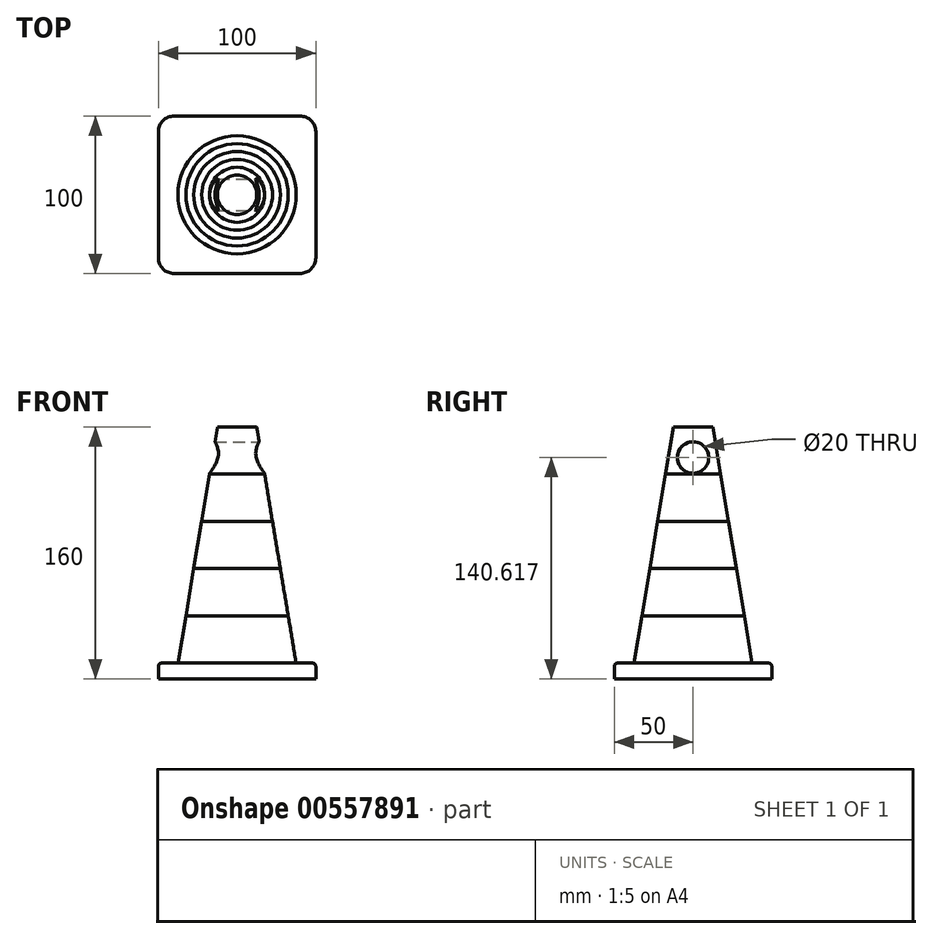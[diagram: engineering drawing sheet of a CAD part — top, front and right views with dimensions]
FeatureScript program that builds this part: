
annotation { "Feature Type Name" : "Feature", "Feature Type Description" : "" }
export const myFeature = defineFeature(function(context is Context, id is Id, definition is map)
    precondition{}
    {
        {
            var Q0;
            Q0=qCreatedBy(makeId("Top.planeOp"),FACE);
            var sketch = newSketch(context, id + "F0", { "sketchPlane" : qUnion([Q0])});
            skLineSegment(sketch, "E0.bottom", {"start": v(-40, 50) * mm, "end": v(40, 50) * mm});
            skLineSegment(sketch, "E0.top", {"start": v(-40, -50) * mm, "end": v(40, -50) * mm});
            skLineSegment(sketch, "E0.left", {"start": v(-50, 40) * mm, "end": v(-50, -40) * mm});
            skLineSegment(sketch, "E0.right", {"start": v(50, 40) * mm, "end": v(50, -40) * mm});
            skPoint(sketch, "E1.visualSharp", {"position": v(-50, 50) * mm});
            skArc(sketch, "E1.filletArc", {"start": v(-40, 50) * mm, "mid": v(-47.07, 47.07) * mm, "end": v(-50, 40) * mm});
            skPoint(sketch, "E2.visualSharp", {"position": v(50, 50) * mm});
            skArc(sketch, "E2.filletArc", {"start": v(50, 40) * mm, "mid": v(47.07, 47.07) * mm, "end": v(40, 50) * mm});
            skPoint(sketch, "E3.visualSharp", {"position": v(50, -50) * mm});
            skArc(sketch, "E3.filletArc", {"start": v(40, -50) * mm, "mid": v(47.07, -47.07) * mm, "end": v(50, -40) * mm});
            skPoint(sketch, "E4.visualSharp", {"position": v(-50, -50) * mm});
            skArc(sketch, "E4.filletArc", {"start": v(-50, -40) * mm, "mid": v(-47.07, -47.07) * mm, "end": v(-40, -50) * mm});
            skSolve(sketch);
        }
        {
            var Q0;
            Q0=makeQuery(id+"F0.imprint","IMPRINT",FACE,{"disambiguationData":[TD([[makeQuery(id+"F0.imprint","IMPRINT",EDGE,{"derivedFrom":sQuery(id+"F0.wireOp",EDGE,"E0.bottom")}),-1.0]])]});
            extrude(context, id + "F1", {"entities" : qUnion([Q0]), "depth" : 10 * mm});
        }
        {
            var Q0;
            Q0=makeQuery(id+"F1.opExtrude","CAP_FACE",FACE,{"disambiguationData":[OSD([sQuery(id+"F0.wireOp",EDGE,"E0.bottom"),sQuery(id+"F0.wireOp",EDGE,"E0.top"),sQuery(id+"F0.wireOp",EDGE,"E0.left"),sQuery(id+"F0.wireOp",EDGE,"E0.right")])],"isStart":false});
            var sketch = newSketch(context, id + "F2", { "sketchPlane" : qUnion([Q0])});
            skLineSegment(sketch, "E5.0.0", {"start": v(-50, 40) * mm, "end": v(-50, -40) * mm});
            skLineSegment(sketch, "E5.0.1", {"start": v(-50, -50) * mm, "end": v(-40, -50) * mm});
            skLineSegment(sketch, "E5.0.2", {"start": v(50, -50) * mm, "end": v(50, 40) * mm});
            skLineSegment(sketch, "E5.0.3", {"start": v(50, 50) * mm, "end": v(-50, 50) * mm});
            skCircle(sketch, "E6", {"center": v(0, 0) * mm, "radius": 37.5 * mm});
            skSolve(sketch);
        }
        {
            var Q0;
            Q0=qCreatedBy(makeId("Top.planeOp"),FACE);
            cPlane(context, id + "F3", {"entities" : qUnion([Q0]), "cplaneType" : CPlaneType.OFFSET, "offset" : 40 * mm, "width" : 150 * mm, "height" : 150 * mm});
        }
        {
            var Q0;
            Q0=qCreatedBy(id+"F3.planeOp",FACE);
            var sketch = newSketch(context, id + "F4", { "sketchPlane" : qUnion([Q0])});
            skCircle(sketch, "E7.0", {"center": v(0, 0) * mm, "radius": 37.5 * mm});
            skCircle(sketch, "E8", {"center": v(0, 0) * mm, "radius": 32.5 * mm});
            skSolve(sketch);
        }
        {
            var Q1;
            Q1=makeQuery(id+"F2.imprint","IMPRINT",FACE,{"disambiguationData":[TD([[makeQuery(id+"F2.imprint","IMPRINT",EDGE,{"derivedFrom":sQuery(id+"F2.wireOp",EDGE,"E6")}),1.0]])]});
            var Q2;
            Q2=makeQuery(id+"F4.imprint","IMPRINT",FACE,{"disambiguationData":[TD([[makeQuery(id+"F4.imprint","IMPRINT",EDGE,{"derivedFrom":sQuery(id+"F4.wireOp",EDGE,"E8")}),1.0]])]});
            loft(context, id + "F5", {"sheetProfilesArray" : [{ "sheetProfileEntities" : qUnion([Q1]) }, { "sheetProfileEntities" : qUnion([Q2]) }]});
        }
        {
            var Q0;
            Q0=qCreatedBy(id+"F3.planeOp",FACE);
            cPlane(context, id + "F6", {"entities" : qUnion([Q0]), "cplaneType" : CPlaneType.OFFSET, "offset" : 30 * mm, "width" : 150 * mm, "height" : 150 * mm});
        }
        {
            var Q0;
            Q0=qCreatedBy(id+"F6.planeOp",FACE);
            var sketch = newSketch(context, id + "F7", { "sketchPlane" : qUnion([Q0])});
            skCircle(sketch, "E9.0.0", {"center": v(0, 0) * mm, "radius": 32.5 * mm});
            skCircle(sketch, "E10", {"center": v(0, 0) * mm, "radius": 27.5 * mm});
            skSolve(sketch);
        }
        {
            var Q1;
            Q1=makeQuery(id+"F5.opLoft","CAP_FACE",FACE,{"disambiguationData":[OSD([makeQuery(id+"F4.imprint","IMPRINT",FACE,{"disambiguationData":[TD([[makeQuery(id+"F4.imprint","IMPRINT",EDGE,{"derivedFrom":sQuery(id+"F4.wireOp",EDGE,"E8")}),1.0]])]})])],"isStart":true});
            var Q2;
            Q2=makeQuery(id+"F7.imprint","IMPRINT",FACE,{"disambiguationData":[TD([[makeQuery(id+"F7.imprint","IMPRINT",EDGE,{"derivedFrom":sQuery(id+"F7.wireOp",EDGE,"E10")}),1.0]])]});
            loft(context, id + "F8", {"sheetProfilesArray" : [{ "sheetProfileEntities" : qUnion([Q1]) }, { "sheetProfileEntities" : qUnion([Q2]) }]});
        }
        {
            var Q0;
            Q0=qCreatedBy(id+"F6.planeOp",FACE);
            cPlane(context, id + "F9", {"entities" : qUnion([Q0]), "cplaneType" : CPlaneType.OFFSET, "offset" : 30 * mm, "width" : 150 * mm, "height" : 150 * mm});
        }
        {
            var Q0;
            Q0=qCreatedBy(id+"F9.planeOp",FACE);
            var sketch = newSketch(context, id + "F10", { "sketchPlane" : qUnion([Q0])});
            skCircle(sketch, "E11.0.0", {"center": v(0, 0) * mm, "radius": 27.5 * mm});
            skCircle(sketch, "E12", {"center": v(0, 0) * mm, "radius": 22.5 * mm});
            skSolve(sketch);
        }
        {
            var Q1;
            Q1=makeQuery(id+"F8.opLoft","CAP_FACE",FACE,{"disambiguationData":[OSD([makeQuery(id+"F7.imprint","IMPRINT",FACE,{"disambiguationData":[TD([[makeQuery(id+"F7.imprint","IMPRINT",EDGE,{"derivedFrom":sQuery(id+"F7.wireOp",EDGE,"E10")}),1.0]])]})])],"isStart":true});
            var Q2;
            Q2=makeQuery(id+"F10.imprint","IMPRINT",FACE,{"disambiguationData":[TD([[makeQuery(id+"F10.imprint","IMPRINT",EDGE,{"derivedFrom":sQuery(id+"F10.wireOp",EDGE,"E12")}),1.0]])]});
            loft(context, id + "F11", {"sheetProfilesArray" : [{ "sheetProfileEntities" : qUnion([Q1]) }, { "sheetProfileEntities" : qUnion([Q2]) }]});
        }
        {
            var Q0;
            Q0=qCreatedBy(id+"F9.planeOp",FACE);
            cPlane(context, id + "F12", {"entities" : qUnion([Q0]), "cplaneType" : CPlaneType.OFFSET, "offset" : 30 * mm, "width" : 150 * mm, "height" : 150 * mm});
        }
        {
            var Q0;
            Q0=qCreatedBy(id+"F12.planeOp",FACE);
            var sketch = newSketch(context, id + "F13", { "sketchPlane" : qUnion([Q0])});
            skCircle(sketch, "E13.0.0", {"center": v(0, 0) * mm, "radius": 22.5 * mm});
            skCircle(sketch, "E14", {"center": v(0, 0) * mm, "radius": 17.5 * mm});
            skSolve(sketch);
        }
        {
            var Q1;
            Q1=makeQuery(id+"F11.opLoft","CAP_FACE",FACE,{"disambiguationData":[OSD([makeQuery(id+"F10.imprint","IMPRINT",FACE,{"disambiguationData":[TD([[makeQuery(id+"F10.imprint","IMPRINT",EDGE,{"derivedFrom":sQuery(id+"F10.wireOp",EDGE,"E12")}),1.0]])]})])],"isStart":true});
            var Q2;
            Q2=makeQuery(id+"F13.imprint","IMPRINT",FACE,{"disambiguationData":[TD([[makeQuery(id+"F13.imprint","IMPRINT",EDGE,{"derivedFrom":sQuery(id+"F13.wireOp",EDGE,"E14")}),1.0]])]});
            loft(context, id + "F14", {"sheetProfilesArray" : [{ "sheetProfileEntities" : qUnion([Q1]) }, { "sheetProfileEntities" : qUnion([Q2]) }]});
        }
        {
            var Q0;
            Q0=qCreatedBy(id+"F12.planeOp",FACE);
            cPlane(context, id + "F15", {"entities" : qUnion([Q0]), "cplaneType" : CPlaneType.OFFSET, "offset" : 30 * mm, "width" : 150 * mm, "height" : 150 * mm});
        }
        {
            var Q0;
            Q0=qCreatedBy(id+"F15.planeOp",FACE);
            var sketch = newSketch(context, id + "F16", { "sketchPlane" : qUnion([Q0])});
            skCircle(sketch, "E15.0.0", {"center": v(0, 0) * mm, "radius": 17.5 * mm});
            skCircle(sketch, "E16", {"center": v(0, 0) * mm, "radius": 12.5 * mm});
            skSolve(sketch);
        }
        {
            var Q1;
            Q1=makeQuery(id+"F14.opLoft","CAP_FACE",FACE,{"disambiguationData":[OSD([makeQuery(id+"F13.imprint","IMPRINT",FACE,{"disambiguationData":[TD([[makeQuery(id+"F13.imprint","IMPRINT",EDGE,{"derivedFrom":sQuery(id+"F13.wireOp",EDGE,"E14")}),1.0]])]})])],"isStart":true});
            var Q2;
            Q2=makeQuery(id+"F16.imprint","IMPRINT",FACE,{"disambiguationData":[TD([[makeQuery(id+"F16.imprint","IMPRINT",EDGE,{"derivedFrom":sQuery(id+"F16.wireOp",EDGE,"E16")}),1.0]])]});
            loft(context, id + "F17", {"sheetProfilesArray" : [{ "sheetProfileEntities" : qUnion([Q1]) }, { "sheetProfileEntities" : qUnion([Q2]) }]});
        }
        {
            var Q0;
            Q0=makeQuery(id+"F1.opExtrude","CAP_EDGE",EDGE,{"disambiguationData":[OSD([sQuery(id+"F0.wireOp",EDGE,"E0.top")])],"isStart":false});
            var Q1;
            Q1=makeQuery(id+"F1.opExtrude","CAP_EDGE",EDGE,{"disambiguationData":[OSD([sQuery(id+"F0.wireOp",EDGE,"E4.filletArc")])],"isStart":false});
            var Q2;
            Q2=makeQuery(id+"F1.opExtrude","CAP_EDGE",EDGE,{"disambiguationData":[OSD([sQuery(id+"F0.wireOp",EDGE,"E0.left")])],"isStart":false});
            var Q3;
            Q3=makeQuery(id+"F1.opExtrude","CAP_EDGE",EDGE,{"disambiguationData":[OSD([sQuery(id+"F0.wireOp",EDGE,"E3.filletArc")])],"isStart":false});
            var Q4;
            Q4=makeQuery(id+"F1.opExtrude","CAP_EDGE",EDGE,{"disambiguationData":[OSD([sQuery(id+"F0.wireOp",EDGE,"E0.right")])],"isStart":false});
            var Q5;
            Q5=makeQuery(id+"F1.opExtrude","CAP_EDGE",EDGE,{"disambiguationData":[OSD([sQuery(id+"F0.wireOp",EDGE,"E2.filletArc")])],"isStart":false});
            var Q6;
            Q6=makeQuery(id+"F1.opExtrude","CAP_EDGE",EDGE,{"disambiguationData":[OSD([sQuery(id+"F0.wireOp",EDGE,"E0.bottom")])],"isStart":false});
            var Q7;
            Q7=makeQuery(id+"F1.opExtrude","CAP_EDGE",EDGE,{"disambiguationData":[OSD([sQuery(id+"F0.wireOp",EDGE,"E1.filletArc")])],"isStart":false});
            fillet(context, id + "F18", {"entities" : qUnion([Q0, Q1, Q2, Q3, Q4, Q5, Q6, Q7]), "radius" : 2 * mm, "tangentPropagation" : true, "allowEdgeOverflow" : false});
        }
        {
            var Q0;
            Q0=makeQuery(id+"F17.opLoft","CAP_FACE",FACE,{"disambiguationData":[OSD([makeQuery(id+"F16.imprint","IMPRINT",FACE,{"disambiguationData":[TD([[makeQuery(id+"F16.imprint","IMPRINT",EDGE,{"derivedFrom":sQuery(id+"F16.wireOp",EDGE,"E16")}),1.0]])]})])],"isStart":true});
            var sketch = newSketch(context, id + "F19", { "sketchPlane" : qUnion([Q0])});
            skCircle(sketch, "E17.0.0", {"center": v(0, 0) * mm, "radius": 12.5 * mm});
            skCircle(sketch, "E18", {"center": v(0, 0) * mm, "radius": 7.5 * mm});
            skSolve(sketch);
        }
        {
            var Q0;
            Q0=qCreatedBy(makeId("Right.planeOp"),FACE);
            var sketch = newSketch(context, id + "F20", { "sketchPlane" : qUnion([Q0])});
            skCircle(sketch, "E19", {"center": v(0, 140.62) * mm, "radius": 10 * mm});
            skSolve(sketch);
        }
        {
            var Q0;
            Q0 = qSketchRegion(id + "F20", true);
            extrude(context, id + "F21", {"entities" : qUnion([Q0]), "operationType" : NewBodyOperationType.REMOVE, "endBound" : BoundingType.SYMMETRIC, "oppositeDirection" : true, "depth" : 60 * mm, "offsetDistance" : 25 * mm});
        }
    });
